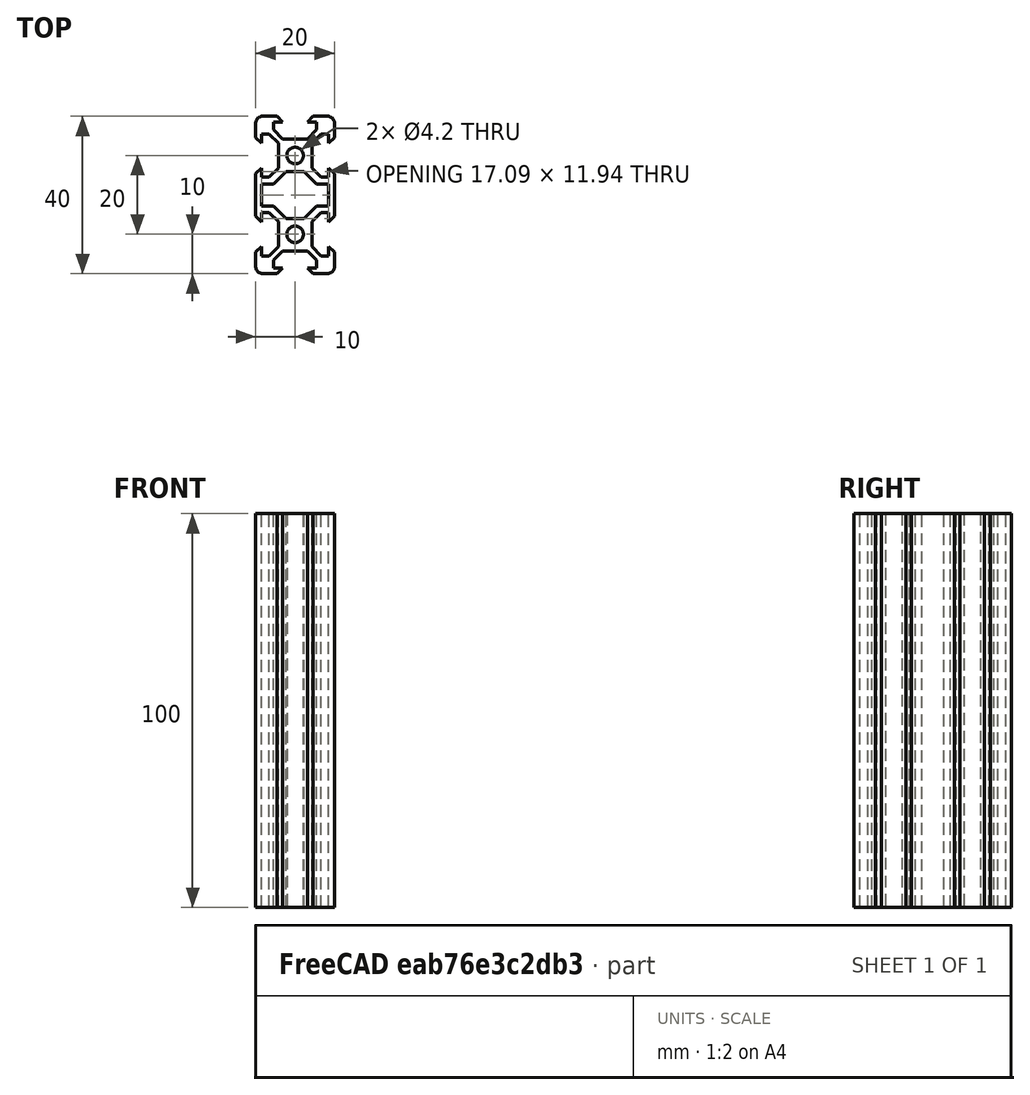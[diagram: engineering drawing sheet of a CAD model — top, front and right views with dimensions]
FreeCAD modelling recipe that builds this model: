
FCSTD DOCUMENT  (FreeCAD 0.19R24267 +99 (Git))
Label: Vslot 2040 Parametrique
License: All rights reserved
LicenseURL: http://en.wikipedia.org/wiki/All_rights_reserved
objects: Sketcher::SketchObject×3, Spreadsheet::Sheet×1, PartDesign::Pad×1, PartDesign::Body×1, App::Part×1
note: 6 computed .brp shape members not serialized (recipe doc carries the construction recipe); baked Part::Feature solids carry a one-line shape summary decoded from their .brp

FEATURE [Sketcher::SketchObject] Sketch
  FullyConstrained = false
  MapMode = 5
  Support = -> [XY_Plane001]
  sketch-geometry (44):
    g0: Circle CenterX=0 CenterY=-10 CenterZ=0 NormalX=0 NormalY=0 NormalZ=1 AngleXU=0 Radius=2.1
    g1: LineSegment StartX=10 StartY=0 StartZ=0 EndX=10 EndY=-5.42 EndZ=0
    g2: LineSegment StartX=10 StartY=-5.42 StartZ=0 EndX=8.545 EndY=-6.875 EndZ=0
    g3: LineSegment StartX=8.545 StartY=-6.875 StartZ=0 EndX=8.545 EndY=-4.5 EndZ=0
    g4: LineSegment StartX=8.545 StartY=-4.5 StartZ=0 EndX=6.56066 EndY=-4.5 EndZ=0
    g5: LineSegment StartX=6.56066 StartY=-4.5 StartZ=0 EndX=4.245 EndY=-6.81566 EndZ=0
    g6: LineSegment StartX=4.245 StartY=-6.81566 StartZ=0 EndX=4.245 EndY=-13.1843 EndZ=0
    g7: LineSegment StartX=4.245 StartY=-13.1843 StartZ=0 EndX=6.56066 EndY=-15.5 EndZ=0
    g8: LineSegment StartX=6.56066 StartY=-15.5 StartZ=0 EndX=8.545 EndY=-15.5 EndZ=0
    g9: LineSegment StartX=8.545 StartY=-15.5 StartZ=0 EndX=8.545 EndY=-13.125 EndZ=0
    g10: LineSegment StartX=8.545 StartY=-13.125 StartZ=0 EndX=10 EndY=-14.58 EndZ=0
    g11: LineSegment StartX=10 StartY=-14.58 StartZ=0 EndX=10 EndY=-18.2 EndZ=0
    g12: LineSegment StartX=8.2 StartY=-20 StartZ=0 EndX=4.58 EndY=-20 EndZ=0
    g13: LineSegment StartX=4.58 StartY=-20 StartZ=0 EndX=3.125 EndY=-18.545 EndZ=0
    g14: LineSegment StartX=3.125 StartY=-18.545 StartZ=0 EndX=5.5 EndY=-18.545 EndZ=0
    g15: LineSegment StartX=5.5 StartY=-18.545 StartZ=0 EndX=5.5 EndY=-16.5607 EndZ=0
    g16: LineSegment StartX=5.5 StartY=-16.5607 StartZ=0 EndX=3.18434 EndY=-14.245 EndZ=0
    g17: LineSegment StartX=3.18434 StartY=-14.245 StartZ=0 EndX=-3.18434 EndY=-14.245 EndZ=0
    g18: LineSegment StartX=-3.18434 StartY=-14.245 StartZ=0 EndX=-5.5 EndY=-16.5607 EndZ=0
    g19: LineSegment StartX=-5.5 StartY=-16.5607 StartZ=0 EndX=-5.5 EndY=-18.545 EndZ=0
    g20: LineSegment StartX=-5.5 StartY=-18.545 StartZ=0 EndX=-3.125 EndY=-18.545 EndZ=0
    g21: LineSegment StartX=-3.125 StartY=-18.545 StartZ=0 EndX=-4.58 EndY=-20 EndZ=0
    g22: LineSegment StartX=-4.58 StartY=-20 StartZ=0 EndX=-8.2 EndY=-20 EndZ=0
    g23: LineSegment StartX=-10 StartY=-18.2 StartZ=0 EndX=-10 EndY=-14.58 EndZ=0
    g24: LineSegment StartX=-10 StartY=-14.58 StartZ=0 EndX=-8.545 EndY=-13.125 EndZ=0
    g25: LineSegment StartX=-8.545 StartY=-13.125 StartZ=0 EndX=-8.545 EndY=-15.5 EndZ=0
    g26: LineSegment StartX=-8.545 StartY=-15.5 StartZ=0 EndX=-6.56066 EndY=-15.5 EndZ=0
    g27: LineSegment StartX=-6.56066 StartY=-15.5 StartZ=0 EndX=-4.245 EndY=-13.1843 EndZ=0
    g28: LineSegment StartX=-4.245 StartY=-13.1843 StartZ=0 EndX=-4.245 EndY=-6.81566 EndZ=0
    g29: LineSegment StartX=-4.245 StartY=-6.81566 StartZ=0 EndX=-6.56066 EndY=-4.5 EndZ=0
    g30: LineSegment StartX=-6.56066 StartY=-4.5 StartZ=0 EndX=-8.545 EndY=-4.5 EndZ=0
    g31: LineSegment StartX=-8.545 StartY=-4.5 StartZ=0 EndX=-8.545 EndY=-6.875 EndZ=0
    g32: LineSegment StartX=-8.545 StartY=-6.875 StartZ=0 EndX=-10 EndY=-5.42 EndZ=0
    g33: LineSegment StartX=-10 StartY=-5.42 StartZ=0 EndX=-10 EndY=0 EndZ=0
    g34: ArcOfCircle CenterX=-8.2 CenterY=-18.2 CenterZ=0 NormalX=0 NormalY=0 NormalZ=1 AngleXU=0 Radius=1.8 StartAngle=3.14159 EndAngle=4.71239
    g35: ArcOfCircle CenterX=8.2 CenterY=-18.2 CenterZ=0 NormalX=0 NormalY=0 NormalZ=1 AngleXU=0 Radius=1.8 StartAngle=4.71239 EndAngle=6.28319
    g36: LineSegment StartX=-10 StartY=-10 StartZ=0 EndX=10 EndY=-10 EndZ=0
    g37: LineSegment StartX=-8.545 StartY=0 StartZ=0 EndX=-8.545 EndY=-2.7884 EndZ=0
    g38: LineSegment StartX=-8.545 StartY=-2.7884 StartZ=0 EndX=-5.42795 EndY=-2.7884 EndZ=0
    g39: LineSegment StartX=-5.42795 StartY=-2.7884 StartZ=0 EndX=-2.24866 EndY=-5.96768 EndZ=0
    g40: LineSegment StartX=-2.24866 StartY=-5.96768 StartZ=0 EndX=2.24866 EndY=-5.96768 EndZ=0
    g41: LineSegment StartX=2.24866 StartY=-5.96768 StartZ=0 EndX=5.42795 EndY=-2.7884 EndZ=0
    g42: LineSegment StartX=5.42795 StartY=-2.7884 StartZ=0 EndX=8.545 EndY=-2.7884 EndZ=0
    g43: LineSegment StartX=8.545 StartY=-2.7884 StartZ=0 EndX=8.545 EndY=0 EndZ=0
  constraints (111):
    c: PointOnObject(g0,g-2)
    c: Radius(g0) = 2.1
    c: PointOnObject(g1,g-1)
    c: Coincident(g1,g2)
    c: Coincident(g2,g3)
    c: Coincident(g3,g4)
    c: Horizontal(g4)
    c: Coincident(g4,g5)
    c: Coincident(g5,g6)
    c: Coincident(g6,g7)
    c: Coincident(g7,g8)
    c: Horizontal(g8)
    c: Coincident(g8,g9)
    c: Coincident(g9,g10)
    c: Coincident(g10,g11)
    c: Coincident(g13,g14)
    c: Horizontal(g14)
    c: Coincident(g14,g15)
    c: Vertical(g15)
    c: Coincident(g15,g16)
    c: Coincident(g16,g17)
    c: Coincident(g17,g18)
    c: Coincident(g18,g19)
    c: Vertical(g19)
    c: Coincident(g19,g20)
    c: Coincident(g20,g21)
    c: Coincident(g21,g22)
    c: Coincident(g23,g24)
    c: Coincident(g24,g25)
    c: Coincident(g25,g26)
    c: Horizontal(g26)
    c: Coincident(g26,g27)
    c: Coincident(g27,g28)
    c: Coincident(g28,g29)
    c: Coincident(g29,g30)
    c: Horizontal(g30)
    c: Coincident(g30,g31)
    c: Coincident(g31,g32)
    c: Coincident(g32,g33)
    c: PointOnObject(g33,g-1)
    c: Tangent(g22,g34) = 1.5708
    c: Tangent(g23,g34) = 1.5708
    c: Tangent(g12,g35) = 1.5708
    c: Tangent(g11,g35) = 1.5708
    c: Tangent(g22,g12)
    c: Symmetric(g17,g16,g-2)
    c: Coincident(g13,g12)
    c: Angle(g21,g13) = 1.5708
    c: Symmetric(g21,g12,g-2)
    c: Symmetric(g19,g14,g-2)
    c: Angle(g18,g16) = 1.5708
    c: Angle(g10,g2) = 1.5708
    c: Angle(g32,g24) = 1.5708
    c: Angle(g7,g5) = 1.5708
    c: Tangent(g9,g3)
    c: Tangent(g1,g11)
    c: Tangent(g31,g25)
    c: Tangent(g23,g33)
    c: Angle(g29,g27) = 1.5708
    c: Radius(g35) = 1.8
    c: DistanceX(g20,g13) = 6.25
    c: DistanceX(g21,g12) = 9.16
    c: Symmetric(g13,g20,g-2)
    c: DistanceX(g19,g14) = 11
    c: DistanceX(g23,g11) = 20
    c: Symmetric(g23,g11,g-2)
    c: DistanceY(g20,g17) = 4.3
    c: DistanceX(g25,g27) = 4.3
    c: Symmetric(g36,g36,g-2)
    c: DistanceX(g36,g36) = 20
    c: Symmetric(g23,g32,g36)
    c: Symmetric(g31,g24,g36)
    c: Symmetric(g30,g25,g36)
    c: Symmetric(g28,g27,g36)
    c: DistanceY(g23,g32) = 9.16
    c: Equal(g19,g15)
    c: DistanceY(g24,g31) = 6.25
    c: DistanceY(g25,g30) = 11
    c: Equal(g30,g26)
    c: PointOnObject(g0,g36)
    c: Equal(g27,g18)
    c: Parallel(g16,g7)
    c: Symmetric(g6,g5,g36)
    c: Symmetric(g1,g10,g36)
    c: DistanceY(g8,g3) = 11
    c: Symmetric(g8,g3,g36)
    c: Symmetric(g2,g9,g36)
    c: DistanceY(g9,g2) = 6.25
    c: DistanceY(g10,g1) = 9.16
    c: DistanceX(g6,g8) = 4.3
    c: Equal(g16,g7)
    c: DistanceY(g21,g36) = 10
    c: Distance(g27,g17) = 1.5
    c: DistanceY(g36,g-1) = 10
    c: PointOnObject(g37,g-1)
    c: Vertical(g37)
    c: Coincident(g37,g38)
    c: Horizontal(g38)
    c: Coincident(g38,g39)
    c: Coincident(g39,g40)
    c: Coincident(g40,g41)
    c: Coincident(g41,g42)
    c: Horizontal(g42)
    c: Coincident(g42,g43)
    c: PointOnObject(g43,g-1)
    c: Vertical(g43)
    c: Tangent(g37,g31)
    c: Tangent(g43,g3)
    c: Symmetric(g41,g38,g-2)
    c: Symmetric(g39,g40,g-2)
    c: Parallel(g29,g39)
FEATURE [Sketcher::SketchObject] MirroredSketch
  FullyConstrained = false
  sketch-geometry (44):
    g0: Circle CenterX=0 CenterY=10 CenterZ=0 NormalX=0 NormalY=0 NormalZ=1 AngleXU=0 Radius=2.1
    g1: LineSegment StartX=10 StartY=0 StartZ=0 EndX=10 EndY=5.42 EndZ=0
    g2: LineSegment StartX=10 StartY=5.42 StartZ=0 EndX=8.545 EndY=6.875 EndZ=0
    g3: LineSegment StartX=8.545 StartY=6.875 StartZ=0 EndX=8.545 EndY=4.5 EndZ=0
    g4: LineSegment StartX=8.545 StartY=4.5 StartZ=0 EndX=6.56066 EndY=4.5 EndZ=0
    g5: LineSegment StartX=6.56066 StartY=4.5 StartZ=0 EndX=4.245 EndY=6.81566 EndZ=0
    g6: LineSegment StartX=4.245 StartY=6.81566 StartZ=0 EndX=4.245 EndY=13.1843 EndZ=0
    g7: LineSegment StartX=4.245 StartY=13.1843 StartZ=0 EndX=6.56066 EndY=15.5 EndZ=0
    g8: LineSegment StartX=6.56066 StartY=15.5 StartZ=0 EndX=8.545 EndY=15.5 EndZ=0
    g9: LineSegment StartX=8.545 StartY=15.5 StartZ=0 EndX=8.545 EndY=13.125 EndZ=0
    g10: LineSegment StartX=8.545 StartY=13.125 StartZ=0 EndX=10 EndY=14.58 EndZ=0
    g11: LineSegment StartX=10 StartY=14.58 StartZ=0 EndX=10 EndY=18.2 EndZ=0
    g12: LineSegment StartX=8.2 StartY=20 StartZ=0 EndX=4.58 EndY=20 EndZ=0
    g13: LineSegment StartX=4.58 StartY=20 StartZ=0 EndX=3.125 EndY=18.545 EndZ=0
    g14: LineSegment StartX=3.125 StartY=18.545 StartZ=0 EndX=5.5 EndY=18.545 EndZ=0
    g15: LineSegment StartX=5.5 StartY=18.545 StartZ=0 EndX=5.5 EndY=16.5607 EndZ=0
    g16: LineSegment StartX=5.5 StartY=16.5607 StartZ=0 EndX=3.18434 EndY=14.245 EndZ=0
    g17: LineSegment StartX=3.18434 StartY=14.245 StartZ=0 EndX=-3.18434 EndY=14.245 EndZ=0
    g18: LineSegment StartX=-3.18434 StartY=14.245 StartZ=0 EndX=-5.5 EndY=16.5607 EndZ=0
    g19: LineSegment StartX=-5.5 StartY=16.5607 StartZ=0 EndX=-5.5 EndY=18.545 EndZ=0
    g20: LineSegment StartX=-5.5 StartY=18.545 StartZ=0 EndX=-3.125 EndY=18.545 EndZ=0
    g21: LineSegment StartX=-3.125 StartY=18.545 StartZ=0 EndX=-4.58 EndY=20 EndZ=0
    g22: LineSegment StartX=-4.58 StartY=20 StartZ=0 EndX=-8.2 EndY=20 EndZ=0
    g23: LineSegment StartX=-10 StartY=18.2 StartZ=0 EndX=-10 EndY=14.58 EndZ=0
    g24: LineSegment StartX=-10 StartY=14.58 StartZ=0 EndX=-8.545 EndY=13.125 EndZ=0
    g25: LineSegment StartX=-8.545 StartY=13.125 StartZ=0 EndX=-8.545 EndY=15.5 EndZ=0
    g26: LineSegment StartX=-8.545 StartY=15.5 StartZ=0 EndX=-6.56066 EndY=15.5 EndZ=0
    g27: LineSegment StartX=-6.56066 StartY=15.5 StartZ=0 EndX=-4.245 EndY=13.1843 EndZ=0
    g28: LineSegment StartX=-4.245 StartY=13.1843 StartZ=0 EndX=-4.245 EndY=6.81566 EndZ=0
    g29: LineSegment StartX=-4.245 StartY=6.81566 StartZ=0 EndX=-6.56066 EndY=4.5 EndZ=0
    g30: LineSegment StartX=-6.56066 StartY=4.5 StartZ=0 EndX=-8.545 EndY=4.5 EndZ=0
    g31: LineSegment StartX=-8.545 StartY=4.5 StartZ=0 EndX=-8.545 EndY=6.875 EndZ=0
    g32: LineSegment StartX=-8.545 StartY=6.875 StartZ=0 EndX=-10 EndY=5.42 EndZ=0
    g33: LineSegment StartX=-10 StartY=5.42 StartZ=0 EndX=-10 EndY=0 EndZ=0
    g34: ArcOfCircle CenterX=-8.2 CenterY=18.2 CenterZ=0 NormalX=0 NormalY=0 NormalZ=1 AngleXU=0 Radius=1.8 StartAngle=1.5708 EndAngle=3.14159
    g35: ArcOfCircle CenterX=8.2 CenterY=18.2 CenterZ=0 NormalX=0 NormalY=0 NormalZ=1 AngleXU=0 Radius=1.8 StartAngle=0 EndAngle=1.5708
    g36: LineSegment StartX=-10 StartY=10 StartZ=0 EndX=10 EndY=10 EndZ=0
    g37: LineSegment StartX=-8.545 StartY=0 StartZ=0 EndX=-8.545 EndY=2.7884 EndZ=0
    g38: LineSegment StartX=-8.545 StartY=2.7884 StartZ=0 EndX=-5.42795 EndY=2.7884 EndZ=0
    g39: LineSegment StartX=-5.42795 StartY=2.7884 StartZ=0 EndX=-2.24866 EndY=5.96768 EndZ=0
    g40: LineSegment StartX=-2.24866 StartY=5.96768 StartZ=0 EndX=2.24866 EndY=5.96768 EndZ=0
    g41: LineSegment StartX=2.24866 StartY=5.96768 StartZ=0 EndX=5.42795 EndY=2.7884 EndZ=0
    g42: LineSegment StartX=5.42795 StartY=2.7884 StartZ=0 EndX=8.545 EndY=2.7884 EndZ=0
    g43: LineSegment StartX=8.545 StartY=2.7884 StartZ=0 EndX=8.545 EndY=0 EndZ=0
  constraints (82):
    c: Radius(g0) = 2.1
    c: Coincident(g1,g2)
    c: Coincident(g2,g3)
    c: Coincident(g3,g4)
    c: Horizontal(g4)
    c: Coincident(g4,g5)
    c: Coincident(g5,g6)
    c: Coincident(g6,g7)
    c: Coincident(g7,g8)
    c: Horizontal(g8)
    c: Coincident(g8,g9)
    c: Coincident(g9,g10)
    c: Coincident(g10,g11)
    c: Coincident(g13,g14)
    c: Horizontal(g14)
    c: Coincident(g14,g15)
    c: Vertical(g15)
    c: Coincident(g15,g16)
    c: Coincident(g16,g17)
    c: Coincident(g17,g18)
    c: Coincident(g18,g19)
    c: Vertical(g19)
    c: Coincident(g19,g20)
    c: Coincident(g20,g21)
    c: Coincident(g21,g22)
    c: Coincident(g23,g24)
    c: Coincident(g24,g25)
    c: Coincident(g25,g26)
    c: Horizontal(g26)
    c: Coincident(g26,g27)
    c: Coincident(g27,g28)
    c: Coincident(g28,g29)
    c: Coincident(g29,g30)
    c: Horizontal(g30)
    c: Coincident(g30,g31)
    c: Coincident(g31,g32)
    c: Coincident(g32,g33)
    c: Tangent(g22,g34) = -1.5708
    c: Tangent(g23,g34) = -1.5708
    c: Tangent(g12,g35) = -1.5708
    c: Tangent(g11,g35) = -1.5708
    c: Tangent(g22,g12)
    c: Coincident(g13,g12)
    c: Angle(g21,g13) = -1.5708
    c: Angle(g18,g16) = -1.5708
    c: Angle(g10,g2) = -1.5708
    c: Angle(g32,g24) = -1.5708
    c: Angle(g7,g5) = -1.5708
    c: Tangent(g9,g3)
    c: Tangent(g1,g11)
    c: Tangent(g31,g25)
    c: Tangent(g23,g33)
    c: Angle(g29,g27) = -1.5708
    c: Radius(g35) = 1.8
    c: Symmetric(g23,g32,g36)
    c: Symmetric(g31,g24,g36)
    c: Symmetric(g30,g25,g36)
    c: Symmetric(g28,g27,g36)
    c: Equal(g19,g15)
    c: Equal(g30,g26)
    c: PointOnObject(g0,g36)
    c: Equal(g27,g18)
    c: Parallel(g16,g7)
    c: Symmetric(g6,g5,g36)
    c: Symmetric(g1,g10,g36)
    c: Symmetric(g8,g3,g36)
    c: Symmetric(g2,g9,g36)
    c: Equal(g16,g7)
    c: Distance(g27,g17) = 1.5
    c: Vertical(g37)
    c: Coincident(g37,g38)
    c: Horizontal(g38)
    c: Coincident(g38,g39)
    c: Coincident(g39,g40)
    c: Coincident(g40,g41)
    c: Coincident(g41,g42)
    c: Horizontal(g42)
    c: Coincident(g42,g43)
    c: Vertical(g43)
    c: Tangent(g37,g31)
    c: Tangent(g43,g3)
    c: Parallel(g29,g39)
FEATURE [Sketcher::SketchObject] Sketch001
  FullyConstrained = false
  sketch-geometry (88):
    g0: Circle CenterX=0 CenterY=-10 CenterZ=0 NormalX=0 NormalY=0 NormalZ=1 AngleXU=0 Radius=2.1
    g1: LineSegment StartX=10 StartY=0 StartZ=0 EndX=10 EndY=-5.42 EndZ=0
    g2: LineSegment StartX=10 StartY=-5.42 StartZ=0 EndX=8.545 EndY=-6.875 EndZ=0
    g3: LineSegment StartX=8.545 StartY=-6.875 StartZ=0 EndX=8.545 EndY=-4.5 EndZ=0
    g4: LineSegment StartX=8.545 StartY=-4.5 StartZ=0 EndX=6.56066 EndY=-4.5 EndZ=0
    g5: LineSegment StartX=6.56066 StartY=-4.5 StartZ=0 EndX=4.245 EndY=-6.81566 EndZ=0
    g6: LineSegment StartX=4.245 StartY=-6.81566 StartZ=0 EndX=4.245 EndY=-13.1843 EndZ=0
    g7: LineSegment StartX=4.245 StartY=-13.1843 StartZ=0 EndX=6.56066 EndY=-15.5 EndZ=0
    g8: LineSegment StartX=6.56066 StartY=-15.5 StartZ=0 EndX=8.545 EndY=-15.5 EndZ=0
    g9: LineSegment StartX=8.545 StartY=-15.5 StartZ=0 EndX=8.545 EndY=-13.125 EndZ=0
    g10: LineSegment StartX=8.545 StartY=-13.125 StartZ=0 EndX=10 EndY=-14.58 EndZ=0
    g11: LineSegment StartX=10 StartY=-14.58 StartZ=0 EndX=10 EndY=-18.2 EndZ=0
    g12: LineSegment StartX=8.2 StartY=-20 StartZ=0 EndX=4.58 EndY=-20 EndZ=0
    g13: LineSegment StartX=4.58 StartY=-20 StartZ=0 EndX=3.125 EndY=-18.545 EndZ=0
    g14: LineSegment StartX=3.125 StartY=-18.545 StartZ=0 EndX=5.5 EndY=-18.545 EndZ=0
    g15: LineSegment StartX=5.5 StartY=-18.545 StartZ=0 EndX=5.5 EndY=-16.5607 EndZ=0
    g16: LineSegment StartX=5.5 StartY=-16.5607 StartZ=0 EndX=3.18434 EndY=-14.245 EndZ=0
    g17: LineSegment StartX=3.18434 StartY=-14.245 StartZ=0 EndX=-3.18434 EndY=-14.245 EndZ=0
    g18: LineSegment StartX=-3.18434 StartY=-14.245 StartZ=0 EndX=-5.5 EndY=-16.5607 EndZ=0
    g19: LineSegment StartX=-5.5 StartY=-16.5607 StartZ=0 EndX=-5.5 EndY=-18.545 EndZ=0
    g20: LineSegment StartX=-5.5 StartY=-18.545 StartZ=0 EndX=-3.125 EndY=-18.545 EndZ=0
    g21: LineSegment StartX=-3.125 StartY=-18.545 StartZ=0 EndX=-4.58 EndY=-20 EndZ=0
    g22: LineSegment StartX=-4.58 StartY=-20 StartZ=0 EndX=-8.2 EndY=-20 EndZ=0
    g23: LineSegment StartX=-10 StartY=-18.2 StartZ=0 EndX=-10 EndY=-14.58 EndZ=0
    g24: LineSegment StartX=-10 StartY=-14.58 StartZ=0 EndX=-8.545 EndY=-13.125 EndZ=0
    g25: LineSegment StartX=-8.545 StartY=-13.125 StartZ=0 EndX=-8.545 EndY=-15.5 EndZ=0
    g26: LineSegment StartX=-8.545 StartY=-15.5 StartZ=0 EndX=-6.56066 EndY=-15.5 EndZ=0
    g27: LineSegment StartX=-6.56066 StartY=-15.5 StartZ=0 EndX=-4.245 EndY=-13.1843 EndZ=0
    g28: LineSegment StartX=-4.245 StartY=-13.1843 StartZ=0 EndX=-4.245 EndY=-6.81566 EndZ=0
    g29: LineSegment StartX=-4.245 StartY=-6.81566 StartZ=0 EndX=-6.56066 EndY=-4.5 EndZ=0
    g30: LineSegment StartX=-6.56066 StartY=-4.5 StartZ=0 EndX=-8.545 EndY=-4.5 EndZ=0
    g31: LineSegment StartX=-8.545 StartY=-4.5 StartZ=0 EndX=-8.545 EndY=-6.875 EndZ=0
    g32: LineSegment StartX=-8.545 StartY=-6.875 StartZ=0 EndX=-10 EndY=-5.42 EndZ=0
    g33: LineSegment StartX=-10 StartY=-5.42 StartZ=0 EndX=-10 EndY=0 EndZ=0
    g34: ArcOfCircle CenterX=-8.2 CenterY=-18.2 CenterZ=0 NormalX=0 NormalY=0 NormalZ=1 AngleXU=0 Radius=1.8 StartAngle=3.14159 EndAngle=4.71239
    g35: ArcOfCircle CenterX=8.2 CenterY=-18.2 CenterZ=0 NormalX=0 NormalY=0 NormalZ=1 AngleXU=0 Radius=1.8 StartAngle=4.71239 EndAngle=6.28319
    g36: LineSegment StartX=-10 StartY=-10 StartZ=0 EndX=10 EndY=-10 EndZ=0
    g37: LineSegment StartX=-8.545 StartY=0 StartZ=0 EndX=-8.545 EndY=-2.7884 EndZ=0
    g38: LineSegment StartX=-8.545 StartY=-2.7884 StartZ=0 EndX=-5.42795 EndY=-2.7884 EndZ=0
    g39: LineSegment StartX=-5.42795 StartY=-2.7884 StartZ=0 EndX=-2.24866 EndY=-5.96768 EndZ=0
    g40: LineSegment StartX=-2.24866 StartY=-5.96768 StartZ=0 EndX=2.24866 EndY=-5.96768 EndZ=0
    g41: LineSegment StartX=2.24866 StartY=-5.96768 StartZ=0 EndX=5.42795 EndY=-2.7884 EndZ=0
    g42: LineSegment StartX=5.42795 StartY=-2.7884 StartZ=0 EndX=8.545 EndY=-2.7884 EndZ=0
    g43: LineSegment StartX=8.545 StartY=-2.7884 StartZ=0 EndX=8.545 EndY=0 EndZ=0
    g44: Circle CenterX=0 CenterY=10 CenterZ=0 NormalX=0 NormalY=0 NormalZ=1 AngleXU=0 Radius=2.1
    g45: LineSegment StartX=10 StartY=0 StartZ=0 EndX=10 EndY=5.42 EndZ=0
    g46: LineSegment StartX=10 StartY=5.42 StartZ=0 EndX=8.545 EndY=6.875 EndZ=0
    g47: LineSegment StartX=8.545 StartY=6.875 StartZ=0 EndX=8.545 EndY=4.5 EndZ=0
    g48: LineSegment StartX=8.545 StartY=4.5 StartZ=0 EndX=6.56066 EndY=4.5 EndZ=0
    g49: LineSegment StartX=6.56066 StartY=4.5 StartZ=0 EndX=4.245 EndY=6.81566 EndZ=0
    g50: LineSegment StartX=4.245 StartY=6.81566 StartZ=0 EndX=4.245 EndY=13.1843 EndZ=0
    g51: LineSegment StartX=4.245 StartY=13.1843 StartZ=0 EndX=6.56066 EndY=15.5 EndZ=0
    g52: LineSegment StartX=6.56066 StartY=15.5 StartZ=0 EndX=8.545 EndY=15.5 EndZ=0
    g53: LineSegment StartX=8.545 StartY=15.5 StartZ=0 EndX=8.545 EndY=13.125 EndZ=0
    g54: LineSegment StartX=8.545 StartY=13.125 StartZ=0 EndX=10 EndY=14.58 EndZ=0
    g55: LineSegment StartX=10 StartY=14.58 StartZ=0 EndX=10 EndY=18.2 EndZ=0
    g56: LineSegment StartX=8.2 StartY=20 StartZ=0 EndX=4.58 EndY=20 EndZ=0
    g57: LineSegment StartX=4.58 StartY=20 StartZ=0 EndX=3.125 EndY=18.545 EndZ=0
    g58: LineSegment StartX=3.125 StartY=18.545 StartZ=0 EndX=5.5 EndY=18.545 EndZ=0
    g59: LineSegment StartX=5.5 StartY=18.545 StartZ=0 EndX=5.5 EndY=16.5607 EndZ=0
    g60: LineSegment StartX=5.5 StartY=16.5607 StartZ=0 EndX=3.18434 EndY=14.245 EndZ=0
    g61: LineSegment StartX=3.18434 StartY=14.245 StartZ=0 EndX=-3.18434 EndY=14.245 EndZ=0
    g62: LineSegment StartX=-3.18434 StartY=14.245 StartZ=0 EndX=-5.5 EndY=16.5607 EndZ=0
    g63: LineSegment StartX=-5.5 StartY=16.5607 StartZ=0 EndX=-5.5 EndY=18.545 EndZ=0
    g64: LineSegment StartX=-5.5 StartY=18.545 StartZ=0 EndX=-3.125 EndY=18.545 EndZ=0
    g65: LineSegment StartX=-3.125 StartY=18.545 StartZ=0 EndX=-4.58 EndY=20 EndZ=0
    g66: LineSegment StartX=-4.58 StartY=20 StartZ=0 EndX=-8.2 EndY=20 EndZ=0
    g67: LineSegment StartX=-10 StartY=18.2 StartZ=0 EndX=-10 EndY=14.58 EndZ=0
    g68: LineSegment StartX=-10 StartY=14.58 StartZ=0 EndX=-8.545 EndY=13.125 EndZ=0
    g69: LineSegment StartX=-8.545 StartY=13.125 StartZ=0 EndX=-8.545 EndY=15.5 EndZ=0
    g70: LineSegment StartX=-8.545 StartY=15.5 StartZ=0 EndX=-6.56066 EndY=15.5 EndZ=0
    g71: LineSegment StartX=-6.56066 StartY=15.5 StartZ=0 EndX=-4.245 EndY=13.1843 EndZ=0
    g72: LineSegment StartX=-4.245 StartY=13.1843 StartZ=0 EndX=-4.245 EndY=6.81566 EndZ=0
    g73: LineSegment StartX=-4.245 StartY=6.81566 StartZ=0 EndX=-6.56066 EndY=4.5 EndZ=0
    g74: LineSegment StartX=-6.56066 StartY=4.5 StartZ=0 EndX=-8.545 EndY=4.5 EndZ=0
    g75: LineSegment StartX=-8.545 StartY=4.5 StartZ=0 EndX=-8.545 EndY=6.875 EndZ=0
    g76: LineSegment StartX=-8.545 StartY=6.875 StartZ=0 EndX=-10 EndY=5.42 EndZ=0
    g77: LineSegment StartX=-10 StartY=5.42 StartZ=0 EndX=-10 EndY=0 EndZ=0
    g78: ArcOfCircle CenterX=-8.2 CenterY=18.2 CenterZ=0 NormalX=0 NormalY=0 NormalZ=1 AngleXU=0 Radius=1.8 StartAngle=1.5708 EndAngle=3.14159
    g79: ArcOfCircle CenterX=8.2 CenterY=18.2 CenterZ=0 NormalX=0 NormalY=0 NormalZ=1 AngleXU=0 Radius=1.8 StartAngle=0 EndAngle=1.5708
    g80: LineSegment StartX=-10 StartY=10 StartZ=0 EndX=10 EndY=10 EndZ=0
    g81: LineSegment StartX=-8.545 StartY=0 StartZ=0 EndX=-8.545 EndY=2.7884 EndZ=0
    g82: LineSegment StartX=-8.545 StartY=2.7884 StartZ=0 EndX=-5.42795 EndY=2.7884 EndZ=0
    g83: LineSegment StartX=-5.42795 StartY=2.7884 StartZ=0 EndX=-2.24866 EndY=5.96768 EndZ=0
    g84: LineSegment StartX=-2.24866 StartY=5.96768 StartZ=0 EndX=2.24866 EndY=5.96768 EndZ=0
    g85: LineSegment StartX=2.24866 StartY=5.96768 StartZ=0 EndX=5.42795 EndY=2.7884 EndZ=0
    g86: LineSegment StartX=5.42795 StartY=2.7884 StartZ=0 EndX=8.545 EndY=2.7884 EndZ=0
    g87: LineSegment StartX=8.545 StartY=2.7884 StartZ=0 EndX=8.545 EndY=0 EndZ=0
  constraints (193):
    c: PointOnObject(g0,g-2)
    c: Radius(g0) = 2.1
    c: PointOnObject(g1,g-1)
    c: Coincident(g1,g2)
    c: Coincident(g2,g3)
    c: Coincident(g3,g4)
    c: Horizontal(g4)
    c: Coincident(g4,g5)
    c: Coincident(g5,g6)
    c: Coincident(g6,g7)
    c: Coincident(g7,g8)
    c: Horizontal(g8)
    c: Coincident(g8,g9)
    c: Coincident(g9,g10)
    c: Coincident(g10,g11)
    c: Coincident(g13,g14)
    c: Horizontal(g14)
    c: Coincident(g14,g15)
    c: Vertical(g15)
    c: Coincident(g15,g16)
    c: Coincident(g16,g17)
    c: Coincident(g17,g18)
    c: Coincident(g18,g19)
    c: Vertical(g19)
    c: Coincident(g19,g20)
    c: Coincident(g20,g21)
    c: Coincident(g21,g22)
    c: Coincident(g23,g24)
    c: Coincident(g24,g25)
    c: Coincident(g25,g26)
    c: Horizontal(g26)
    c: Coincident(g26,g27)
    c: Coincident(g27,g28)
    c: Coincident(g28,g29)
    c: Coincident(g29,g30)
    c: Horizontal(g30)
    c: Coincident(g30,g31)
    c: Coincident(g31,g32)
    c: Coincident(g32,g33)
    c: PointOnObject(g33,g-1)
    c: Tangent(g22,g34) = 1.5708
    c: Tangent(g23,g34) = 1.5708
    c: Tangent(g12,g35) = 1.5708
    c: Tangent(g11,g35) = 1.5708
    c: Tangent(g22,g12)
    c: Symmetric(g17,g16,g-2)
    c: Coincident(g13,g12)
    c: Angle(g21,g13) = 1.5708
    c: Symmetric(g21,g12,g-2)
    c: Symmetric(g19,g14,g-2)
    c: Angle(g18,g16) = 1.5708
    c: Angle(g10,g2) = 1.5708
    c: Angle(g32,g24) = 1.5708
    c: Angle(g7,g5) = 1.5708
    c: Tangent(g9,g3)
    c: Tangent(g1,g11)
    c: Tangent(g31,g25)
    c: Tangent(g23,g33)
    c: Angle(g29,g27) = 1.5708
    c: Radius(g35) = 1.8
    c: DistanceX(g20,g13) = 6.25
    c: DistanceX(g21,g12) = 9.16
    c: Symmetric(g13,g20,g-2)
    c: DistanceX(g19,g14) = 11
    c: DistanceX(g23,g11) = 20
    c: Symmetric(g23,g11,g-2)
    c: DistanceY(g20,g17) = 4.3
    c: DistanceX(g25,g27) = 4.3
    c: Symmetric(g36,g36,g-2)
    c: DistanceX(g36,g36) = 20
    c: Symmetric(g23,g32,g36)
    c: Symmetric(g31,g24,g36)
    c: Symmetric(g30,g25,g36)
    c: Symmetric(g28,g27,g36)
    c: DistanceY(g23,g32) = 9.16
    c: Equal(g19,g15)
    c: DistanceY(g24,g31) = 6.25
    c: DistanceY(g25,g30) = 11
    c: Equal(g30,g26)
    c: PointOnObject(g0,g36)
    c: Equal(g27,g18)
    c: Parallel(g16,g7)
    c: Symmetric(g6,g5,g36)
    c: Symmetric(g1,g10,g36)
    c: DistanceY(g8,g3) = 11
    c: Symmetric(g8,g3,g36)
    c: Symmetric(g2,g9,g36)
    c: DistanceY(g9,g2) = 6.25
    c: DistanceY(g10,g1) = 9.16
    c: DistanceX(g6,g8) = 4.3
    c: Equal(g16,g7)
    c: DistanceY(g21,g36) = 10
    c: Distance(g27,g17) = 1.5
    c: DistanceY(g36,g-1) = 10
    c: PointOnObject(g37,g-1)
    c: Vertical(g37)
    c: Coincident(g37,g38)
    c: Horizontal(g38)
    c: Coincident(g38,g39)
    c: Coincident(g39,g40)
    c: Coincident(g40,g41)
    c: Coincident(g41,g42)
    c: Horizontal(g42)
    c: Coincident(g42,g43)
    c: PointOnObject(g43,g-1)
    c: Vertical(g43)
    c: Tangent(g37,g31)
    c: Tangent(g43,g3)
    c: Symmetric(g41,g38,g-2)
    c: Symmetric(g39,g40,g-2)
    c: Parallel(g29,g39)
    c: Radius(g44) = 2.1
    c: Coincident(g45,g46)
    c: Coincident(g46,g47)
    c: Coincident(g47,g48)
    c: Horizontal(g48)
    c: Coincident(g48,g49)
    c: Coincident(g49,g50)
    c: Coincident(g50,g51)
    c: Coincident(g51,g52)
    c: Horizontal(g52)
    c: Coincident(g52,g53)
    c: Coincident(g53,g54)
    c: Coincident(g54,g55)
    c: Coincident(g57,g58)
    c: Horizontal(g58)
    c: Coincident(g58,g59)
    c: Vertical(g59)
    c: Coincident(g59,g60)
    c: Coincident(g60,g61)
    c: Coincident(g61,g62)
    c: Coincident(g62,g63)
    c: Vertical(g63)
    c: Coincident(g63,g64)
    c: Coincident(g64,g65)
    c: Coincident(g65,g66)
    c: Coincident(g67,g68)
    c: Coincident(g68,g69)
    c: Coincident(g69,g70)
    c: Horizontal(g70)
    c: Coincident(g70,g71)
    c: Coincident(g71,g72)
    c: Coincident(g72,g73)
    c: Coincident(g73,g74)
    c: Horizontal(g74)
    c: Coincident(g74,g75)
    c: Coincident(g75,g76)
    c: Coincident(g76,g77)
    c: Tangent(g66,g78) = -1.5708
    c: Tangent(g67,g78) = -1.5708
    c: Tangent(g56,g79) = -1.5708
    c: Tangent(g55,g79) = -1.5708
    c: Tangent(g66,g56)
    c: Coincident(g57,g56)
    c: Angle(g65,g57) = -1.5708
    c: Angle(g62,g60) = -1.5708
    c: Angle(g54,g46) = -1.5708
    c: Angle(g76,g68) = -1.5708
    c: Angle(g51,g49) = -1.5708
    c: Tangent(g53,g47)
    c: Tangent(g45,g55)
    c: Tangent(g75,g69)
    c: Tangent(g67,g77)
    c: Angle(g73,g71) = -1.5708
    c: Radius(g79) = 1.8
    c: Symmetric(g67,g76,g80)
    c: Symmetric(g75,g68,g80)
    c: Symmetric(g74,g69,g80)
    c: Symmetric(g72,g71,g80)
    c: Equal(g63,g59)
    c: Equal(g74,g70)
    c: PointOnObject(g44,g80)
    c: Equal(g71,g62)
    c: Parallel(g60,g51)
    c: Symmetric(g50,g49,g80)
    c: Symmetric(g45,g54,g80)
    c: Symmetric(g52,g47,g80)
    c: Symmetric(g46,g53,g80)
    c: Equal(g60,g51)
    c: Distance(g71,g61) = 1.5
    c: Vertical(g81)
    c: Coincident(g81,g82)
    c: Horizontal(g82)
    c: Coincident(g82,g83)
    c: Coincident(g83,g84)
    c: Coincident(g84,g85)
    c: Coincident(g85,g86)
    c: Horizontal(g86)
    c: Coincident(g86,g87)
    c: Vertical(g87)
    c: Tangent(g81,g75)
    c: Tangent(g87,g47)
    c: Parallel(g73,g83)
FEATURE [Spreadsheet::Sheet] Spreadsheet  label="VSlot_parametrique2040"
  cells = A1=Longeur; B1(VSLOT_L)=100
FEATURE [PartDesign::Pad] Pad
  Direction = (1,1,1)
  Length = 100
  Length2 = 100
  Profile = -> Sketch001
  Type = 0
  expr: Length = <<VSlot_parametrique2040>>.VSLOT_L
FEATURE [PartDesign::Body] Body
  Group = -> [Sketch,MirroredSketch,Sketch001,Pad]
  Origin = -> Origin001
  Tip = -> Pad
FEATURE [App::Part] Part  label="Vslot 2040: 100mm"
  Group = -> [Spreadsheet,Body]
  Origin = -> Origin
  expr: Label = <<Vslot 2040: %s>> % +<<VSlot_parametrique2040>>.VSLOT_L + <<mm>>
